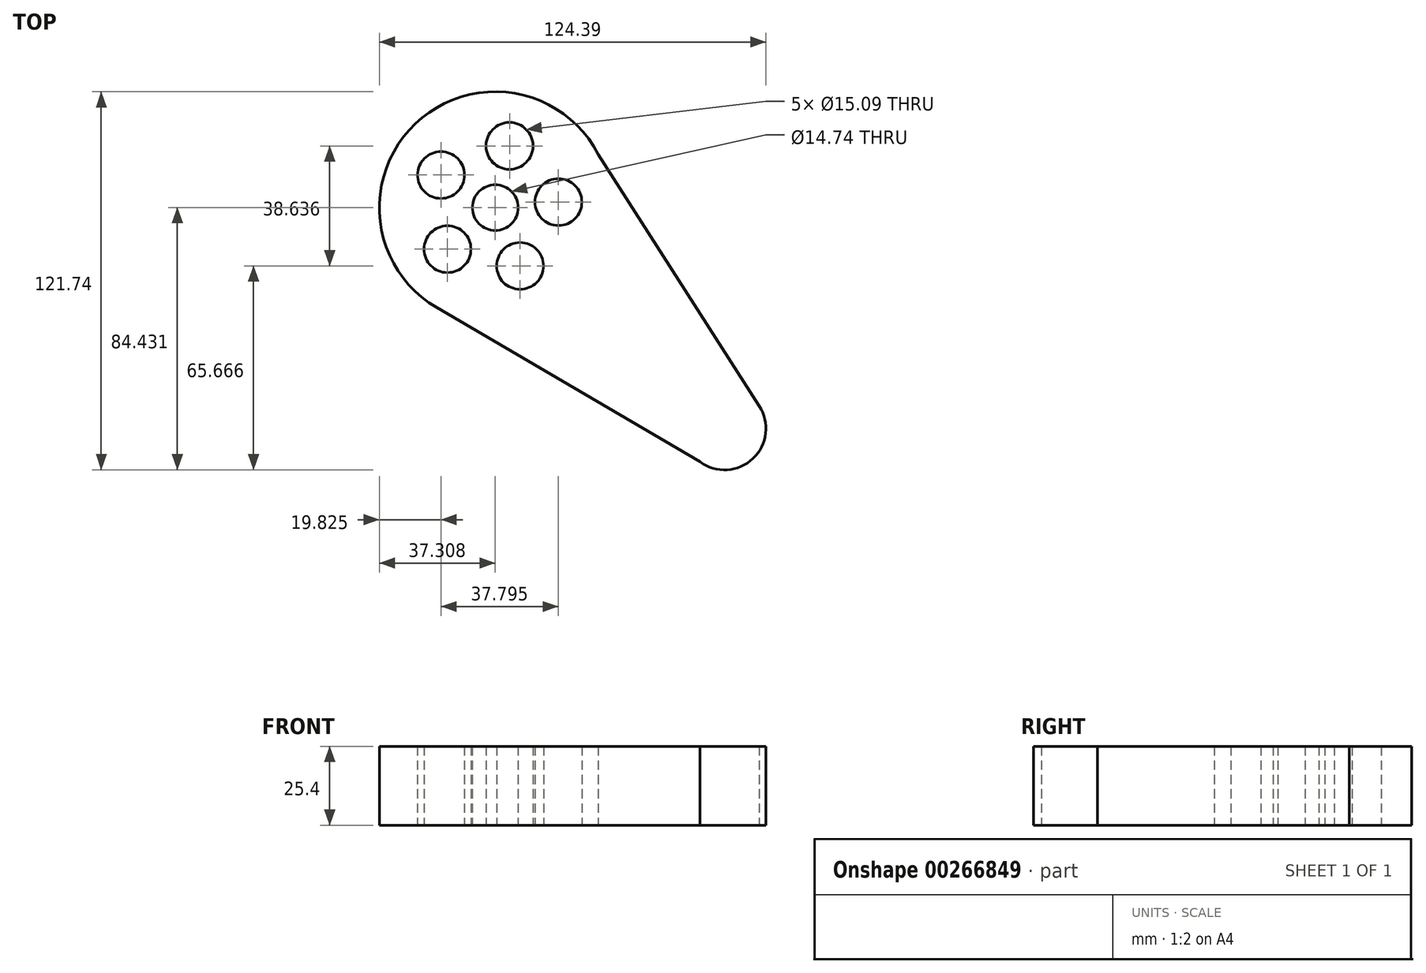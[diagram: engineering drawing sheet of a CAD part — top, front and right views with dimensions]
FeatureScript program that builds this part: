
annotation { "Feature Type Name" : "Feature", "Feature Type Description" : "" }
export const myFeature = defineFeature(function(context is Context, id is Id, definition is map)
    precondition{}
    {
        {
            var Q0;
            Q0=qCreatedBy(makeId("Top.planeOp"),FACE);
            var sketch = newSketch(context, id + "F0", { "sketchPlane" : qUnion([Q0])});
            skCircle(sketch, "E0", {"center": v(-46.8, 52.97) * mm, "radius": 37.3 * mm});
            skCircle(sketch, "E1", {"center": v(26.97, -18.15) * mm, "radius": 13.31 * mm});
            skCircle(sketch, "E2", {"center": v(-42.23, 72.84) * mm, "radius": 7.55 * mm});
            skCircle(sketch, "E3.1.0", {"center": v(-64.29, 63.46) * mm, "radius": 7.55 * mm});
            skCircle(sketch, "E3.2.0", {"center": v(-62.18, 39.59) * mm, "radius": 7.55 * mm});
            skCircle(sketch, "E3.3.0", {"center": v(-38.83, 34.2) * mm, "radius": 7.55 * mm});
            skCircle(sketch, "E3.4.0", {"center": v(-26.5, 54.76) * mm, "radius": 7.55 * mm});
            skPoint(sketch, "E4.center", {"position": v(0, 0) * mm});
            skLineSegment(sketch, "E5", {"start": v(19.06, -28.86) * mm, "end": v(-65.66, 20.78) * mm});
            skCircle(sketch, "E6", {"center": v(-46.8, 52.97) * mm, "radius": 7.37 * mm});
            skLineSegment(sketch, "E7", {"start": v(38.1, -10.86) * mm, "end": v(-17.31, 75.82) * mm});
            skSolve(sketch);
        }
        {
            var Q0;
            Q0 = qSketchRegion(id + "F0", true);
            extrude(context, id + "F1", {"entities" : qUnion([Q0]), "depth" : 25.4 * mm});
        }
    });
